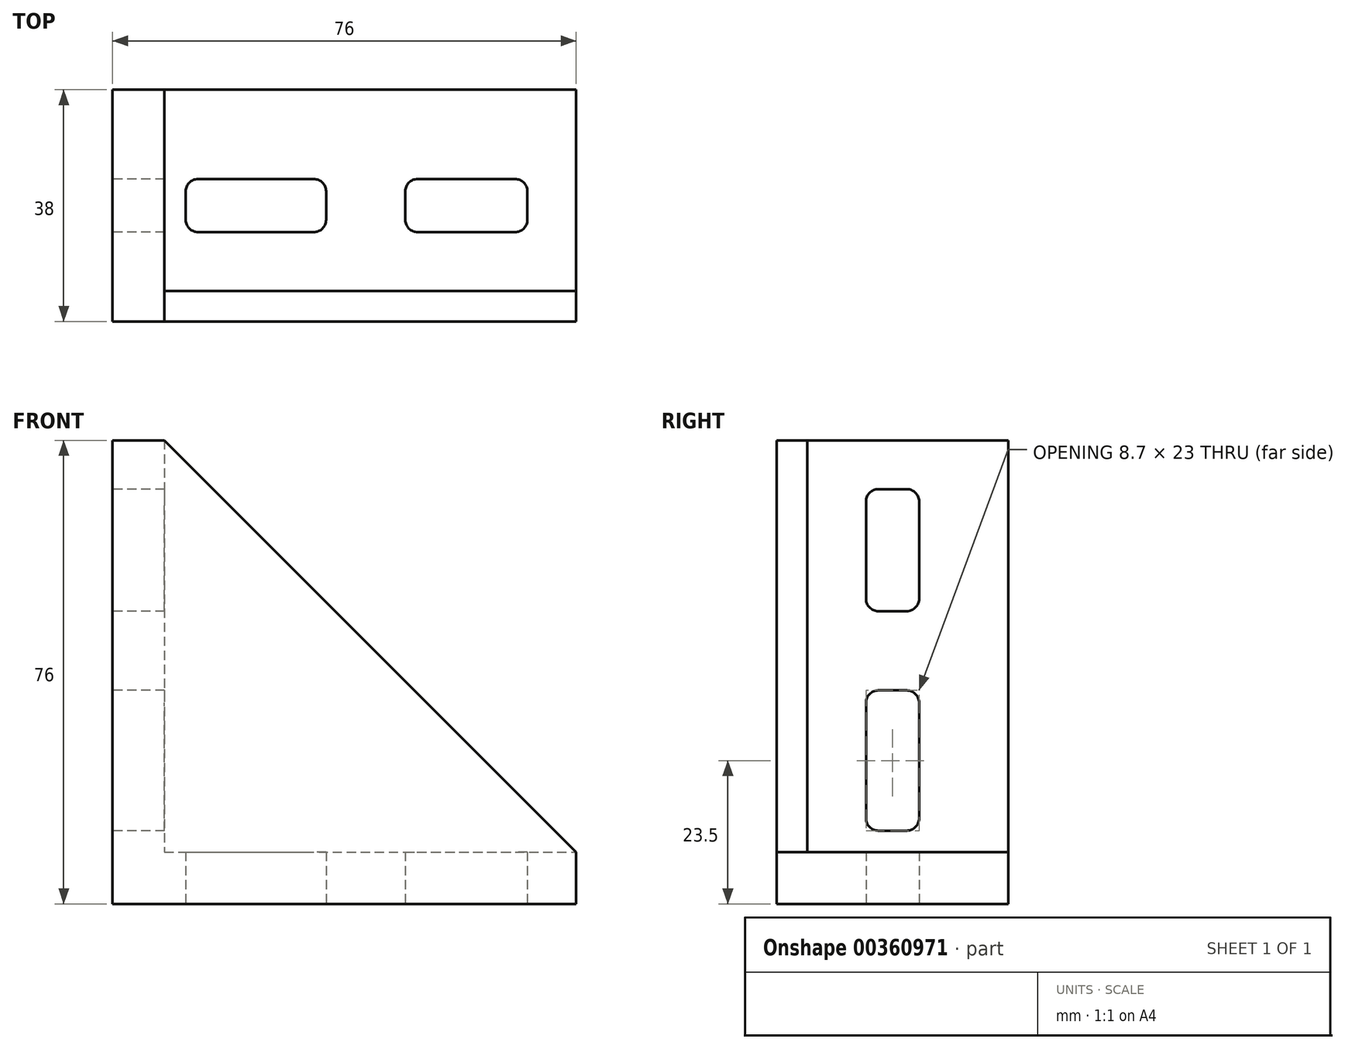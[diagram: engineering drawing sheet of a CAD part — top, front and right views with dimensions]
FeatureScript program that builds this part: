
annotation { "Feature Type Name" : "Feature", "Feature Type Description" : "" }
export const myFeature = defineFeature(function(context is Context, id is Id, definition is map)
    precondition{}
    {
        {
            var Q0;
            Q0=qCreatedBy(makeId("Top.planeOp"),FACE);
            var sketch = newSketch(context, id + "F0", { "sketchPlane" : qUnion([Q0])});
            skLineSegment(sketch, "E0.bottom", {"start": v(38, 19) * mm, "end": v(-38, 19) * mm});
            skLineSegment(sketch, "E0.top", {"start": v(38, -19) * mm, "end": v(-38, -19) * mm});
            skLineSegment(sketch, "E0.left", {"start": v(38, 19) * mm, "end": v(38, -19) * mm});
            skLineSegment(sketch, "E0.right", {"start": v(-38, 19) * mm, "end": v(-38, -19) * mm});
            skPoint(sketch, "E0.middle", {"position": v(0, 0) * mm});
            skPoint(sketch, "E1", {"position": v(-38, 11.4) * mm});
            skPoint(sketch, "E2", {"position": v(-38, -11.4) * mm});
            skSolve(sketch);
        }
        {
            var Q0;
            Q0=makeQuery(id+"F0.imprint","IMPRINT",FACE,{"disambiguationData":[TD([[makeQuery(id+"F0.imprint","IMPRINT",EDGE,{"derivedFrom":sQuery(id+"F0.wireOp",EDGE,"E0.bottom")}),1.0]])]});
            extrude(context, id + "F1", {"entities" : qUnion([Q0]), "depth" : 76 * mm});
        }
        {
            var Q0;
            Q0=makeQuery(id+"F1.opExtrude","SWEPT_FACE",FACE,{"disambiguationData":[OSD([sQuery(id+"F0.wireOp",EDGE,"E0.bottom")])]});
            var sketch = newSketch(context, id + "F2", { "sketchPlane" : qUnion([Q0])});
            skLineSegment(sketch, "E3", {"start": v(38, 76) * mm, "end": v(38, 0) * mm});
            skLineSegment(sketch, "E4", {"start": v(38, 0) * mm, "end": v(-38, 0) * mm});
            skLineSegment(sketch, "E5", {"start": v(-38, 0) * mm, "end": v(-38, 8.5) * mm});
            skLineSegment(sketch, "E6", {"start": v(-38, 8.5) * mm, "end": v(29.5, 76) * mm});
            skLineSegment(sketch, "E7", {"start": v(29.5, 76) * mm, "end": v(38, 76) * mm});
            skLineSegment(sketch, "E8", {"start": v(29.5, 76) * mm, "end": v(29.5, 8.5) * mm});
            skLineSegment(sketch, "E9", {"start": v(29.5, 8.5) * mm, "end": v(-38, 8.5) * mm});
            skSolve(sketch);
        }
        {
            var Q0;
            {var subQ0=sQuery(id+"F2.wireOp",EDGE,"E6");Q0=makeQuery(id+"F2.imprint","IMPRINT",FACE,{"disambiguationData":[TD([[makeQuery(id+"F2.imprint","IMPRINT",EDGE,{"derivedFrom":subQ0}),1.0]])]});}
            extrude(context, id + "F3", {"entities" : qUnion([Q0]), "operationType" : NewBodyOperationType.REMOVE, "endBound" : BoundingType.THROUGH_ALL, "oppositeDirection" : true, "depth" : 25 * mm});
        }
        {
            var Q0;
            Q0=makeQuery(id+"F2.imprint","IMPRINT",FACE,{"disambiguationData":[TD([[makeQuery(id+"F2.imprint","IMPRINT",EDGE,{"derivedFrom":sQuery(id+"F2.wireOp",EDGE,"E6")}),-1.0]])]});
            extrude(context, id + "F4", {"entities" : qUnion([Q0]), "operationType" : NewBodyOperationType.REMOVE, "oppositeDirection" : true, "depth" : 33 * mm});
        }
        {
            var Q0;
            Q0=makeQuery(id+"F1.opExtrude","SWEPT_FACE",FACE,{"disambiguationData":[OSD([sQuery(id+"F0.wireOp",EDGE,"E0.right")])]});
            var sketch = newSketch(context, id + "F5", { "sketchPlane" : qUnion([Q0])});
            skLineSegment(sketch, "E10.bottom", {"start": v(-2.35, 68) * mm, "end": v(2.35, 68) * mm});
            skLineSegment(sketch, "E10.top", {"start": v(-2.35, 48) * mm, "end": v(2.35, 48) * mm});
            skLineSegment(sketch, "E10.left", {"start": v(-4.35, 66) * mm, "end": v(-4.35, 50) * mm});
            skLineSegment(sketch, "E10.right", {"start": v(4.35, 66) * mm, "end": v(4.35, 50) * mm});
            skLineSegment(sketch, "E11.bottom", {"start": v(-2.35, 35) * mm, "end": v(2.35, 35) * mm});
            skLineSegment(sketch, "E11.top", {"start": v(-2.35, 12) * mm, "end": v(2.35, 12) * mm});
            skLineSegment(sketch, "E11.left", {"start": v(-4.35, 33) * mm, "end": v(-4.35, 14) * mm});
            skLineSegment(sketch, "E11.right", {"start": v(4.35, 33) * mm, "end": v(4.35, 14) * mm});
            skLineSegment(sketch, "E12", {"start": v(0, 0) * mm, "end": v(0, 76) * mm, "construction": true});
            skPoint(sketch, "E13.visualSharp", {"position": v(-4.35, 12) * mm});
            skArc(sketch, "E13.filletArc", {"start": v(-4.35, 14) * mm, "mid": v(-3.76, 12.59) * mm, "end": v(-2.35, 12) * mm});
            skPoint(sketch, "E14.visualSharp", {"position": v(-4.35, 35) * mm});
            skArc(sketch, "E14.filletArc", {"start": v(-2.35, 35) * mm, "mid": v(-3.76, 34.41) * mm, "end": v(-4.35, 33) * mm});
            skPoint(sketch, "E15.visualSharp", {"position": v(4.35, 35) * mm});
            skArc(sketch, "E15.filletArc", {"start": v(4.35, 33) * mm, "mid": v(3.76, 34.41) * mm, "end": v(2.35, 35) * mm});
            skPoint(sketch, "E16.visualSharp", {"position": v(4.35, 12) * mm});
            skArc(sketch, "E16.filletArc", {"start": v(2.35, 12) * mm, "mid": v(3.76, 12.59) * mm, "end": v(4.35, 14) * mm});
            skPoint(sketch, "E17.visualSharp", {"position": v(-4.35, 48) * mm});
            skArc(sketch, "E17.filletArc", {"start": v(-4.35, 50) * mm, "mid": v(-3.76, 48.59) * mm, "end": v(-2.35, 48) * mm});
            skPoint(sketch, "E18.visualSharp", {"position": v(4.35, 48) * mm});
            skArc(sketch, "E18.filletArc", {"start": v(2.35, 48) * mm, "mid": v(3.76, 48.59) * mm, "end": v(4.35, 50) * mm});
            skPoint(sketch, "E19.visualSharp", {"position": v(-4.35, 68) * mm});
            skArc(sketch, "E19.filletArc", {"start": v(-2.35, 68) * mm, "mid": v(-3.76, 67.41) * mm, "end": v(-4.35, 66) * mm});
            skPoint(sketch, "E20.visualSharp", {"position": v(4.35, 68) * mm});
            skArc(sketch, "E20.filletArc", {"start": v(4.35, 66) * mm, "mid": v(3.76, 67.41) * mm, "end": v(2.35, 68) * mm});
            skSolve(sketch);
        }
        {
            var Q0;
            Q0=makeQuery(id+"F5.imprint","IMPRINT",FACE,{"disambiguationData":[TD([[makeQuery(id+"F5.imprint","IMPRINT",EDGE,{"derivedFrom":sQuery(id+"F5.wireOp",EDGE,"E10.bottom")}),-1.0]])]});
            var Q1;
            Q1=makeQuery(id+"F5.imprint","IMPRINT",FACE,{"disambiguationData":[TD([[makeQuery(id+"F5.imprint","IMPRINT",EDGE,{"derivedFrom":sQuery(id+"F5.wireOp",EDGE,"E11.bottom")}),-1.0]])]});
            extrude(context, id + "F6", {"entities" : qUnion([Q0, Q1]), "operationType" : NewBodyOperationType.REMOVE, "endBound" : BoundingType.THROUGH_ALL, "oppositeDirection" : true, "depth" : 25 * mm});
        }
        {
            var Q0;
            Q0=makeQuery(id+"F1.opExtrude","CAP_FACE",FACE,{"disambiguationData":[OSD([sQuery(id+"F0.wireOp",EDGE,"E0.bottom"),sQuery(id+"F0.wireOp",EDGE,"E0.top"),sQuery(id+"F0.wireOp",EDGE,"E0.left"),sQuery(id+"F0.wireOp",EDGE,"E0.right")])],"isStart":true});
            var sketch = newSketch(context, id + "F7", { "sketchPlane" : qUnion([Q0])});
            skLineSegment(sketch, "E21.bottom", {"start": v(30, 2.35) * mm, "end": v(30, -2.35) * mm});
            skLineSegment(sketch, "E21.top", {"start": v(10, 2.35) * mm, "end": v(10, -2.35) * mm});
            skLineSegment(sketch, "E21.left", {"start": v(28, 4.35) * mm, "end": v(12, 4.35) * mm});
            skLineSegment(sketch, "E21.right", {"start": v(28, -4.35) * mm, "end": v(12, -4.35) * mm});
            skLineSegment(sketch, "E22.bottom", {"start": v(-3, 2.35) * mm, "end": v(-3, -2.35) * mm});
            skLineSegment(sketch, "E22.top", {"start": v(-26, 2.35) * mm, "end": v(-26, -2.35) * mm});
            skLineSegment(sketch, "E22.left", {"start": v(-5, 4.35) * mm, "end": v(-24, 4.35) * mm});
            skLineSegment(sketch, "E22.right", {"start": v(-5, -4.35) * mm, "end": v(-24, -4.35) * mm});
            skLineSegment(sketch, "E23", {"start": v(-38, 0) * mm, "end": v(38, 0) * mm, "construction": true});
            skPoint(sketch, "E24.visualSharp", {"position": v(-26, 4.35) * mm});
            skArc(sketch, "E24.filletArc", {"start": v(-24, 4.35) * mm, "mid": v(-25.41, 3.76) * mm, "end": v(-26, 2.35) * mm});
            skPoint(sketch, "E25.visualSharp", {"position": v(-3, 4.35) * mm});
            skArc(sketch, "E25.filletArc", {"start": v(-3, 2.35) * mm, "mid": v(-3.59, 3.76) * mm, "end": v(-5, 4.35) * mm});
            skPoint(sketch, "E26.visualSharp", {"position": v(-3, -4.35) * mm});
            skArc(sketch, "E26.filletArc", {"start": v(-5, -4.35) * mm, "mid": v(-3.59, -3.76) * mm, "end": v(-3, -2.35) * mm});
            skPoint(sketch, "E27.visualSharp", {"position": v(-26, -4.35) * mm});
            skArc(sketch, "E27.filletArc", {"start": v(-26, -2.35) * mm, "mid": v(-25.41, -3.76) * mm, "end": v(-24, -4.35) * mm});
            skPoint(sketch, "E28.visualSharp", {"position": v(10, 4.35) * mm});
            skArc(sketch, "E28.filletArc", {"start": v(12, 4.35) * mm, "mid": v(10.59, 3.76) * mm, "end": v(10, 2.35) * mm});
            skPoint(sketch, "E29.visualSharp", {"position": v(10, -4.35) * mm});
            skArc(sketch, "E29.filletArc", {"start": v(10, -2.35) * mm, "mid": v(10.59, -3.76) * mm, "end": v(12, -4.35) * mm});
            skPoint(sketch, "E30.visualSharp", {"position": v(30, 4.35) * mm});
            skArc(sketch, "E30.filletArc", {"start": v(30, 2.35) * mm, "mid": v(29.41, 3.76) * mm, "end": v(28, 4.35) * mm});
            skPoint(sketch, "E31.visualSharp", {"position": v(30, -4.35) * mm});
            skArc(sketch, "E31.filletArc", {"start": v(28, -4.35) * mm, "mid": v(29.41, -3.76) * mm, "end": v(30, -2.35) * mm});
            skSolve(sketch);
        }
        {
            var Q0;
            Q0=makeQuery(id+"F7.imprint","IMPRINT",FACE,{"disambiguationData":[TD([[makeQuery(id+"F7.imprint","IMPRINT",EDGE,{"derivedFrom":sQuery(id+"F7.wireOp",EDGE,"E22.bottom")}),-1.0]])]});
            var Q1;
            Q1=makeQuery(id+"F7.imprint","IMPRINT",FACE,{"disambiguationData":[TD([[makeQuery(id+"F7.imprint","IMPRINT",EDGE,{"derivedFrom":sQuery(id+"F7.wireOp",EDGE,"E21.bottom")}),-1.0]])]});
            extrude(context, id + "F8", {"entities" : qUnion([Q0, Q1]), "operationType" : NewBodyOperationType.REMOVE, "endBound" : BoundingType.THROUGH_ALL, "oppositeDirection" : true, "depth" : 25 * mm});
        }
    });
